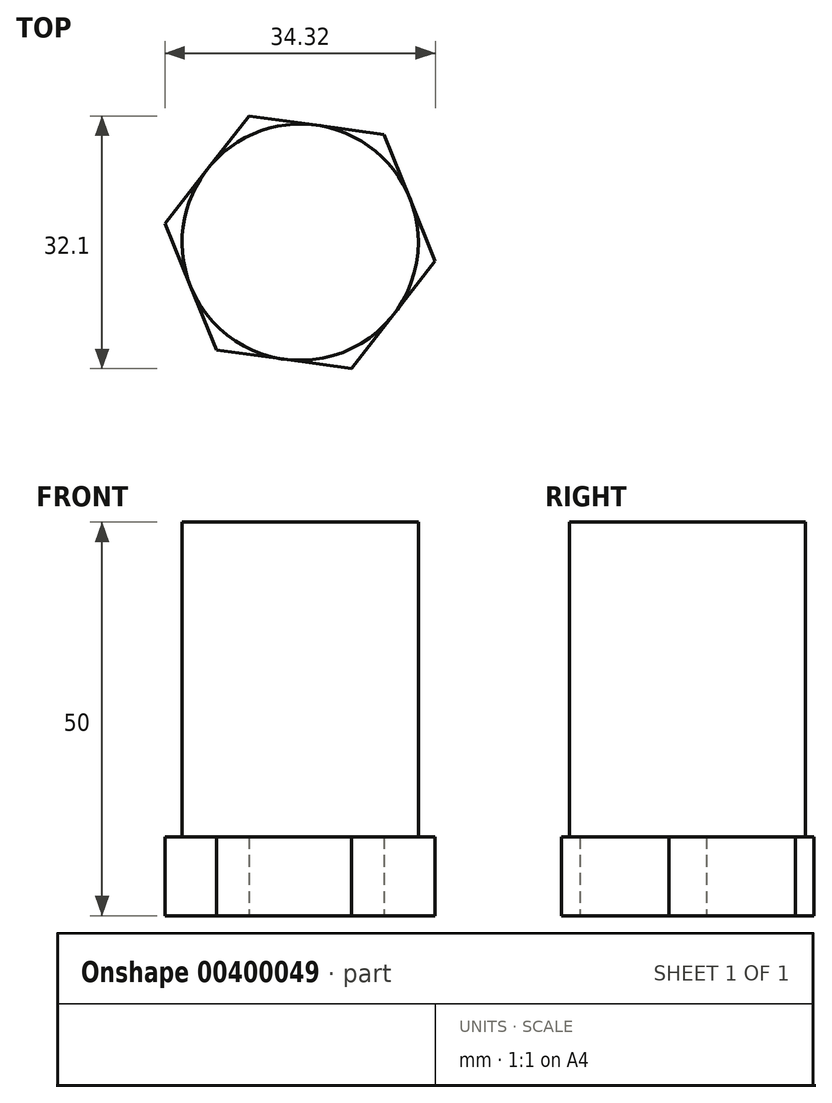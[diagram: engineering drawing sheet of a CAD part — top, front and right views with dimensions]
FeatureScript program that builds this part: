
annotation { "Feature Type Name" : "Feature", "Feature Type Description" : "" }
export const myFeature = defineFeature(function(context is Context, id is Id, definition is map)
    precondition{}
    {
        {
            var Q0;
            Q0=qCreatedBy(makeId("Top.planeOp"),FACE);
            var sketch = newSketch(context, id + "F0", { "sketchPlane" : qUnion([Q0])});
            skCircle(sketch, "E0", {"center": v(0, 0) * mm, "radius": 15 * mm});
            skCircle(sketch, "E1.cCircle", {"center": v(0, 0) * mm, "radius": 15 * mm, "construction": true});
            skLineSegment(sketch, "E1.0", {"start": v(-6.52, 16.05) * mm, "end": v(10.63, 13.67) * mm});
            skLineSegment(sketch, "E1.1", {"start": v(10.63, 13.67) * mm, "end": v(17.16, -2.37) * mm});
            skLineSegment(sketch, "E1.2", {"start": v(17.16, -2.37) * mm, "end": v(6.52, -16.05) * mm});
            skLineSegment(sketch, "E1.3", {"start": v(6.52, -16.05) * mm, "end": v(-10.63, -13.67) * mm});
            skLineSegment(sketch, "E1.4", {"start": v(-10.63, -13.67) * mm, "end": v(-17.16, 2.37) * mm});
            skLineSegment(sketch, "E1.5", {"start": v(-17.16, 2.37) * mm, "end": v(-6.52, 16.05) * mm});
            skPoint(sketch, "E1.0.midPoint", {"position": v(2.06, 14.86) * mm});
            skSolve(sketch);
        }
        {
            var Q0;
            {var subQ0=sQuery(id+"F0.wireOp",EDGE,"E0");var subQ4=makeQuery(id+"F0.imprint","INTERSECT",VERTEX,{"derivedFrom":[subQ0,sQuery(id+"F0.wireOp",EDGE,"E1.0")]});Q0=makeQuery(id+"F0.imprint","IMPRINT",FACE,{"disambiguationData":[TD([[makeQuery(id+"F0.imprint","IMPRINT",EDGE,{"disambiguationData":[TD([[subQ4,1.0]])],"derivedFrom":subQ0}),1.0]])]});}
            extrude(context, id + "F1", {"entities" : qUnion([Q0]), "depth" : 50 * mm});
        }
        {
            var Q0;
            Q0=qSketchRegion(id+"F0",true);
            extrude(context, id + "F2", {"entities" : qUnion([Q0]), "operationType" : NewBodyOperationType.ADD, "depth" : 10 * mm});
        }
    });
